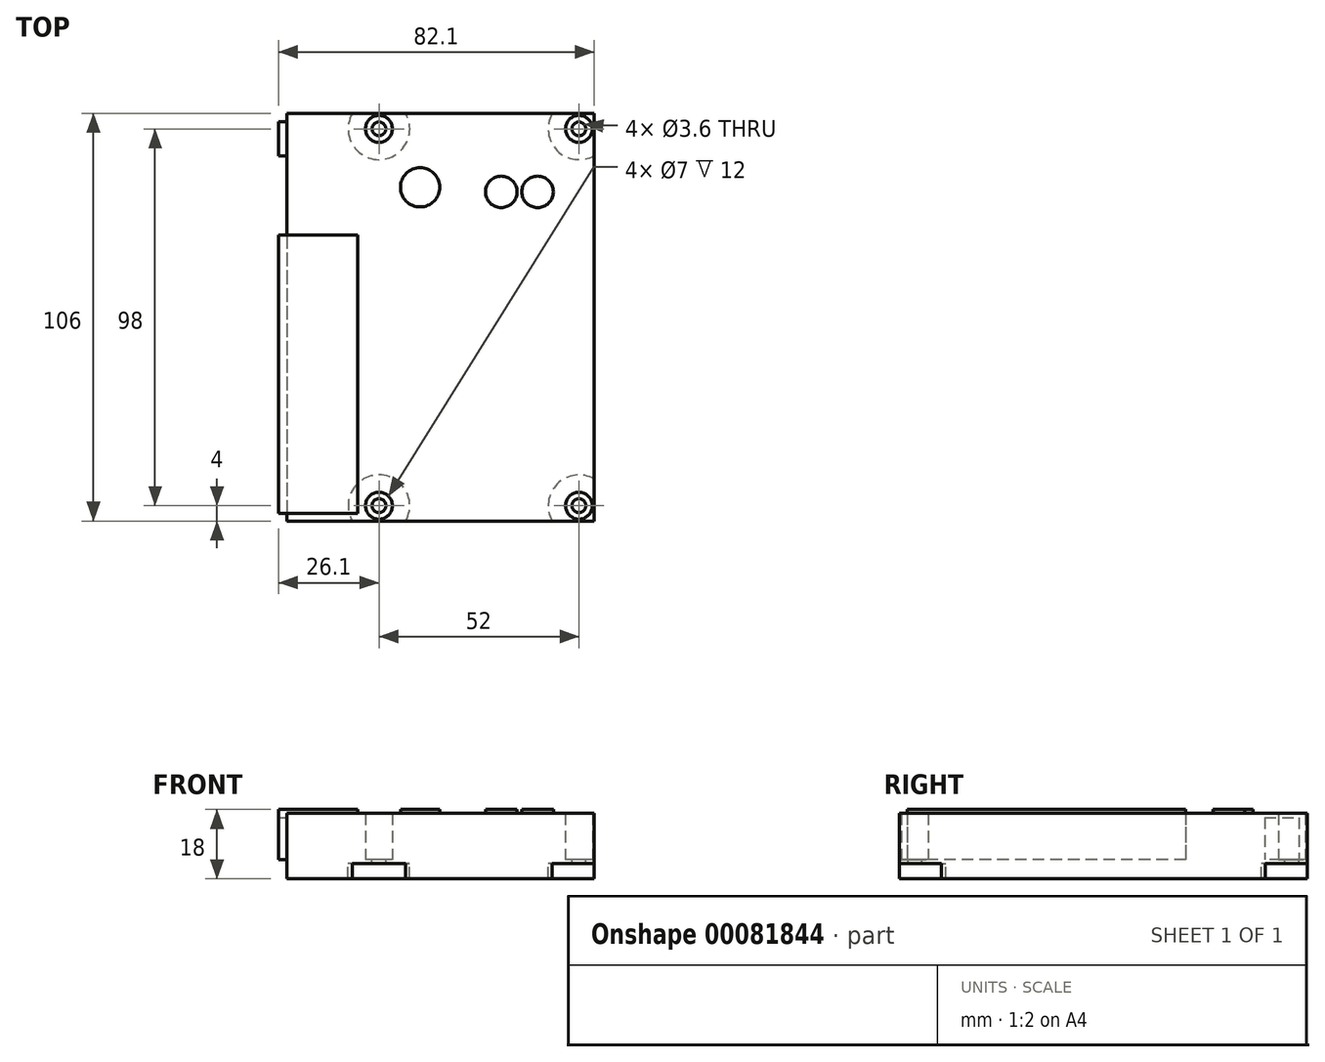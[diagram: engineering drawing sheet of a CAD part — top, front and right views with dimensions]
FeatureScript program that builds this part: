
annotation { "Feature Type Name" : "Feature", "Feature Type Description" : "" }
export const myFeature = defineFeature(function(context is Context, id is Id, definition is map)
    precondition{}
    {
        {
            var Q0;
            Q0=qCreatedBy(makeId("Top.planeOp"),FACE);
            var sketch = newSketch(context, id + "F0", { "sketchPlane" : qUnion([Q0])});
            skLineSegment(sketch, "E0.bottom", {"start": v(-40, 53) * mm, "end": v(40, 53) * mm});
            skLineSegment(sketch, "E0.top", {"start": v(-40, -53) * mm, "end": v(40, -53) * mm});
            skLineSegment(sketch, "E0.left", {"start": v(-40, 53) * mm, "end": v(-40, -53) * mm});
            skLineSegment(sketch, "E0.right", {"start": v(40, 53) * mm, "end": v(40, -53) * mm});
            skCircle(sketch, "E1", {"center": v(-16, 49) * mm, "radius": 1.8 * mm});
            skCircle(sketch, "E2", {"center": v(36, 49) * mm, "radius": 1.8 * mm});
            skCircle(sketch, "E3", {"center": v(-16, -49) * mm, "radius": 1.8 * mm});
            skCircle(sketch, "E4", {"center": v(36, -49) * mm, "radius": 1.8 * mm});
            skSolve(sketch);
        }
        {
            var Q0;
            Q0 = qSketchRegion(id + "F0", true);
            extrude(context, id + "F1", {"entities" : qUnion([Q0]), "oppositeDirection" : true, "depth" : 1 * mm});
        }
        {
            var Q0;
            Q0=makeQuery(id+"F1.opExtrude","CAP_FACE",FACE,{"disambiguationData":[OSD([sQuery(id+"F0.wireOp",EDGE,"E0.bottom"),sQuery(id+"F0.wireOp",EDGE,"E0.top"),sQuery(id+"F0.wireOp",EDGE,"E0.left"),sQuery(id+"F0.wireOp",EDGE,"E0.right"),sQuery(id+"F0.wireOp",EDGE,"E1"),sQuery(id+"F0.wireOp",EDGE,"E2"),sQuery(id+"F0.wireOp",EDGE,"E3"),sQuery(id+"F0.wireOp",EDGE,"E4")])],"isStart":true});
            var sketch = newSketch(context, id + "F2", { "sketchPlane" : qUnion([Q0])});
            skLineSegment(sketch, "E5.bottom", {"start": v(-42.1, 21.4) * mm, "end": v(-21.5, 21.4) * mm});
            skLineSegment(sketch, "E5.top", {"start": v(-42.1, -51) * mm, "end": v(-21.5, -51) * mm});
            skLineSegment(sketch, "E5.left", {"start": v(-42.1, 21.4) * mm, "end": v(-42.1, -51) * mm});
            skLineSegment(sketch, "E5.right", {"start": v(-21.5, 21.4) * mm, "end": v(-21.5, -51) * mm});
            skSolve(sketch);
        }
        {
            var Q0;
            Q0 = qSketchRegion(id + "F2", true);
            extrude(context, id + "F3", {"entities" : qUnion([Q0]), "operationType" : NewBodyOperationType.ADD, "depth" : 13 * mm});
        }
        {
            var Q0;
            Q0=makeQuery(id+"F1.opExtrude","CAP_FACE",FACE,{"disambiguationData":[OSD([sQuery(id+"F0.wireOp",EDGE,"E0.bottom"),sQuery(id+"F0.wireOp",EDGE,"E0.top"),sQuery(id+"F0.wireOp",EDGE,"E0.left"),sQuery(id+"F0.wireOp",EDGE,"E0.right"),sQuery(id+"F0.wireOp",EDGE,"E1"),sQuery(id+"F0.wireOp",EDGE,"E2"),sQuery(id+"F0.wireOp",EDGE,"E3"),sQuery(id+"F0.wireOp",EDGE,"E4")])],"isStart":true});
            var sketch = newSketch(context, id + "F4", { "sketchPlane" : qUnion([Q0])});
            skLineSegment(sketch, "E6.bottom", {"start": v(-42.1, 50.8) * mm, "end": v(-32.1, 50.8) * mm});
            skLineSegment(sketch, "E6.top", {"start": v(-42.1, 41.9) * mm, "end": v(-32.1, 41.9) * mm});
            skLineSegment(sketch, "E6.left", {"start": v(-42.1, 50.8) * mm, "end": v(-42.1, 41.9) * mm});
            skLineSegment(sketch, "E6.right", {"start": v(-32.1, 50.8) * mm, "end": v(-32.1, 41.9) * mm});
            skSolve(sketch);
        }
        {
            var Q0;
            Q0 = qSketchRegion(id + "F4", true);
            extrude(context, id + "F5", {"entities" : qUnion([Q0]), "operationType" : NewBodyOperationType.ADD, "depth" : 10.9 * mm});
        }
        {
            var Q0;
            Q0=makeQuery(id+"F1.opExtrude","CAP_FACE",FACE,{"disambiguationData":[OSD([sQuery(id+"F0.wireOp",EDGE,"E0.bottom"),sQuery(id+"F0.wireOp",EDGE,"E0.top"),sQuery(id+"F0.wireOp",EDGE,"E0.left"),sQuery(id+"F0.wireOp",EDGE,"E0.right"),sQuery(id+"F0.wireOp",EDGE,"E1"),sQuery(id+"F0.wireOp",EDGE,"E2"),sQuery(id+"F0.wireOp",EDGE,"E3"),sQuery(id+"F0.wireOp",EDGE,"E4")])],"isStart":true});
            var sketch = newSketch(context, id + "F6", { "sketchPlane" : qUnion([Q0])});
            skCircle(sketch, "E7", {"center": v(-5.3, 33.8) * mm, "radius": 5.1 * mm});
            skCircle(sketch, "E8", {"center": v(15.8, 32.6) * mm, "radius": 4.1 * mm});
            skCircle(sketch, "E9", {"center": v(25.24, 32.6) * mm, "radius": 4.1 * mm});
            skSolve(sketch);
        }
        {
            var Q0;
            Q0=makeQuery(id+"F6.imprint","IMPRINT",FACE,{"disambiguationData":[TD([[makeQuery(id+"F6.imprint","IMPRINT",EDGE,{"derivedFrom":sQuery(id+"F6.wireOp",EDGE,"E7")}),1.0]])]});
            var Q1;
            Q1=makeQuery(id+"F6.imprint","IMPRINT",FACE,{"disambiguationData":[TD([[makeQuery(id+"F6.imprint","IMPRINT",EDGE,{"derivedFrom":sQuery(id+"F6.wireOp",EDGE,"E8")}),1.0]])]});
            var Q2;
            Q2=makeQuery(id+"F6.imprint","IMPRINT",FACE,{"disambiguationData":[TD([[makeQuery(id+"F6.imprint","IMPRINT",EDGE,{"derivedFrom":sQuery(id+"F6.wireOp",EDGE,"E9")}),1.0]])]});
            extrude(context, id + "F7", {"entities" : qUnion([Q0, Q1, Q2]), "operationType" : NewBodyOperationType.ADD, "depth" : 13 * mm});
        }
        {
            var Q0;
            Q0=makeQuery(id+"F1.opExtrude","CAP_FACE",FACE,{"disambiguationData":[OSD([sQuery(id+"F0.wireOp",EDGE,"E0.bottom"),sQuery(id+"F0.wireOp",EDGE,"E0.top"),sQuery(id+"F0.wireOp",EDGE,"E0.left"),sQuery(id+"F0.wireOp",EDGE,"E0.right"),sQuery(id+"F0.wireOp",EDGE,"E1"),sQuery(id+"F0.wireOp",EDGE,"E2"),sQuery(id+"F0.wireOp",EDGE,"E3"),sQuery(id+"F0.wireOp",EDGE,"E4")])],"isStart":false});
            var sketch = newSketch(context, id + "F8", { "sketchPlane" : qUnion([Q0])});
            skLineSegment(sketch, "E10.0", {"start": v(-40, 53) * mm, "end": v(40, 53) * mm});
            skLineSegment(sketch, "E11.0", {"start": v(40, -53) * mm, "end": v(40, 53) * mm});
            skLineSegment(sketch, "E12.0", {"start": v(-40, -53) * mm, "end": v(40, -53) * mm});
            skLineSegment(sketch, "E13.0", {"start": v(-40, -53) * mm, "end": v(-40, 53) * mm});
            skArc(sketch, "E14", {"start": v(-22.93, 53) * mm, "mid": v(-16, 41) * mm, "end": v(-9.07, 53) * mm});
            skArc(sketch, "E15", {"start": v(29.07, 53) * mm, "mid": v(30.34, 43.34) * mm, "end": v(40, 42.07) * mm});
            skArc(sketch, "E16", {"start": v(40, -42.07) * mm, "mid": v(30.34, -43.34) * mm, "end": v(29.07, -53) * mm});
            skArc(sketch, "E17", {"start": v(-9.07, -53) * mm, "mid": v(-16, -41) * mm, "end": v(-22.93, -53) * mm});
            skSolve(sketch);
        }
        {
            var Q0;
            {var subQ0=sQuery(id+"F8.wireOp",EDGE,"E13.0");Q0=makeQuery(id+"F8.imprint","IMPRINT",FACE,{"disambiguationData":[TD([[makeQuery(id+"F8.imprint","IMPRINT",EDGE,{"derivedFrom":subQ0}),-1.0]])]});}
            extrude(context, id + "F9", {"entities" : qUnion([Q0]), "operationType" : NewBodyOperationType.ADD, "depth" : 4 * mm});
        }
        {
            var Q0;
            Q0=makeQuery(id+"F1.opExtrude","CAP_FACE",FACE,{"disambiguationData":[OSD([sQuery(id+"F0.wireOp",EDGE,"E0.bottom"),sQuery(id+"F0.wireOp",EDGE,"E0.top"),sQuery(id+"F0.wireOp",EDGE,"E0.left"),sQuery(id+"F0.wireOp",EDGE,"E0.right"),sQuery(id+"F0.wireOp",EDGE,"E1"),sQuery(id+"F0.wireOp",EDGE,"E2"),sQuery(id+"F0.wireOp",EDGE,"E3"),sQuery(id+"F0.wireOp",EDGE,"E4")])],"isStart":true});
            var sketch = newSketch(context, id + "F10", { "sketchPlane" : qUnion([Q0])});
            skCircle(sketch, "E18", {"center": v(36, 49) * mm, "radius": 3.5 * mm});
            skCircle(sketch, "E19", {"center": v(-16, 49) * mm, "radius": 3.5 * mm});
            skCircle(sketch, "E20", {"center": v(-16, -49) * mm, "radius": 3.5 * mm});
            skCircle(sketch, "E21", {"center": v(36, -49) * mm, "radius": 3.5 * mm});
            skLineSegment(sketch, "E22.bottom", {"start": v(40, 53) * mm, "end": v(-40, 53) * mm});
            skLineSegment(sketch, "E22.top", {"start": v(40, -53) * mm, "end": v(-40, -53) * mm});
            skLineSegment(sketch, "E22.left", {"start": v(40, 53) * mm, "end": v(40, -53) * mm});
            skLineSegment(sketch, "E22.right", {"start": v(-40, 53) * mm, "end": v(-40, -53) * mm});
            skSolve(sketch);
        }
        {
            var Q0;
            Q0 = qSketchRegion(id + "F10", true);
            extrude(context, id + "F11", {"entities" : qUnion([Q0]), "operationType" : NewBodyOperationType.ADD, "depth" : 12 * mm});
        }
    });
